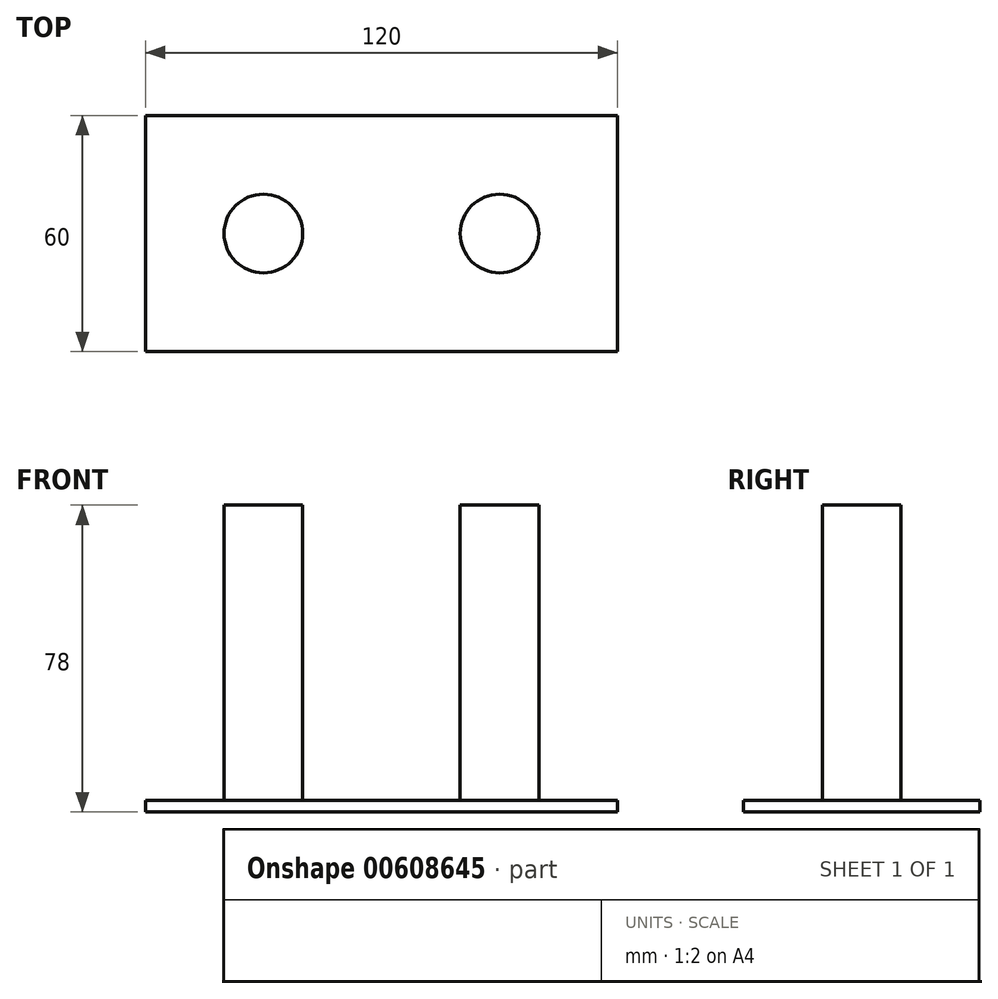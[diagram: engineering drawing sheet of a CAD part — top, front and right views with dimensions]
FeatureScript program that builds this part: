
annotation { "Feature Type Name" : "Feature", "Feature Type Description" : "" }
export const myFeature = defineFeature(function(context is Context, id is Id, definition is map)
    precondition{}
    {
        {
            var Q0;
            Q0=qCreatedBy(makeId("Top.planeOp"),FACE);
            var sketch = newSketch(context, id + "F0", { "sketchPlane" : qUnion([Q0])});
            skCircle(sketch, "E0", {"center": v(0, 0) * mm, "radius": 10 * mm});
            skLineSegment(sketch, "E1", {"start": v(0, 0) * mm, "end": v(-60, 0) * mm, "construction": true});
            skCircle(sketch, "E2", {"center": v(-60, 0) * mm, "radius": 10 * mm});
            skLineSegment(sketch, "E3.bottom", {"start": v(-90, 30) * mm, "end": v(30, 30) * mm});
            skLineSegment(sketch, "E3.top", {"start": v(-90, -30) * mm, "end": v(30, -30) * mm});
            skLineSegment(sketch, "E3.left", {"start": v(-90, 30) * mm, "end": v(-90, -30) * mm});
            skLineSegment(sketch, "E3.right", {"start": v(30, 30) * mm, "end": v(30, -30) * mm});
            skSolve(sketch);
        }
        {
            var Q0;
            Q0=makeQuery(id+"F0.imprint","IMPRINT",FACE,{"disambiguationData":[TD([[makeQuery(id+"F0.imprint","IMPRINT",EDGE,{"derivedFrom":sQuery(id+"F0.wireOp",EDGE,"E0")}),-1.0]])]});
            var Q1;
            Q1=makeQuery(id+"F0.imprint","IMPRINT",FACE,{"disambiguationData":[TD([[makeQuery(id+"F0.imprint","IMPRINT",EDGE,{"derivedFrom":sQuery(id+"F0.wireOp",EDGE,"E2")}),1.0]])]});
            var Q2;
            Q2=makeQuery(id+"F0.imprint","IMPRINT",FACE,{"disambiguationData":[TD([[makeQuery(id+"F0.imprint","IMPRINT",EDGE,{"derivedFrom":sQuery(id+"F0.wireOp",EDGE,"E0")}),1.0]])]});
            extrude(context, id + "F1", {"entities" : qUnion([Q0, Q1, Q2]), "oppositeDirection" : true, "depth" : 3 * mm, "offsetDistance" : 25 * mm});
        }
        {
            var Q0;
            Q0=makeQuery(id+"F0.imprint","IMPRINT",FACE,{"disambiguationData":[TD([[makeQuery(id+"F0.imprint","IMPRINT",EDGE,{"derivedFrom":sQuery(id+"F0.wireOp",EDGE,"E2")}),1.0]])]});
            var Q1;
            Q1=makeQuery(id+"F0.imprint","IMPRINT",FACE,{"disambiguationData":[TD([[makeQuery(id+"F0.imprint","IMPRINT",EDGE,{"derivedFrom":sQuery(id+"F0.wireOp",EDGE,"E0")}),1.0]])]});
            extrude(context, id + "F2", {"entities" : qUnion([Q0, Q1]), "operationType" : NewBodyOperationType.ADD, "depth" : 75 * mm, "offsetDistance" : 25 * mm});
        }
    });
